# Revit family: New Penta
name_source: partatom
category: Equipamento especial
revit_build: Autodesk Revit 2016 (Build: 20150220_1215(x64)
units: mm (PartAtom-declared; Revit-internal decimal feet)

## family parameters
Com base no plano de trabalho = Não
Compartilhado = Não
Corte com vazios quando carregados = Não
Cota do conector redondo = Utilizar diâmetro
Ponto de cálculo do ambiente = Não
Sempre na vertical = Sim
Tipo de parte = Normal

## types (1)
- Tramontina - New Penta 5GX TRI 75
    Classe de Construção = Classe 2
    Código de montagem = 94716/111
    Descrição = Tramontina New Penta  94716/111
    Desenvolvedor = Factory Cursos & Desenvolvimento
    Fabricante = Tramontina
    Frequência = 50 - 60 Hz
    Modelo = Tramontina 94716/111
    Nicho de Instalação = 630 X 470 mm
    Peso Bruto = 10,3 kg
    Peso liquido = 8,5 kg
    Potência Máx Rápido (1X) = 3,00 kW
    Potência Máx Semirrápido (2X) = 1,75 kW
    Potência Máx Tripla chama (1X) = 4,10 kW
    Potência Máx. Auxiliar (1X) = 1,00 kW
    Potência elétrica = 5 kW
    Potência térmica = 11,30 kW
    Rendimento Médio = 63%
    Site do desenvolvedor = www.factorycursos.com.br
    Tensão = 127 -  220 V
    Tipo de imagem = <Nenhum>
    URL = www.tramontina.com.br
